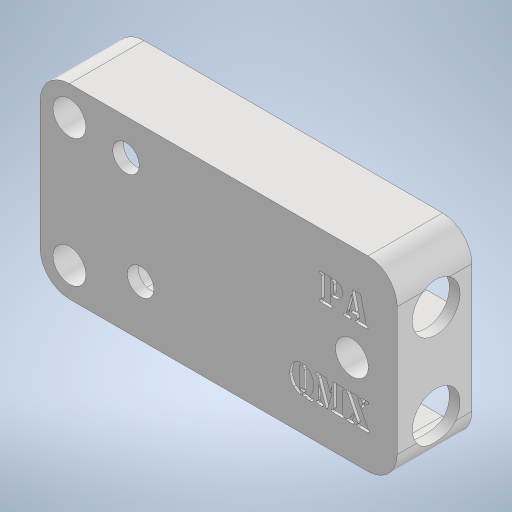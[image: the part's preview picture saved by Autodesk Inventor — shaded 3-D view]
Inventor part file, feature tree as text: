
AUTODESK INVENTOR PART (.ipt)
format: ipt  version: 2023 (Build 270158000, 158)  size: 636,416 bytes
history: native  units: in
note: dims shown in document units (in); Inventor stores cm internally (conversion verified against a paired STEP export)
features: sketch x9, reference x9, extrude x8, projected_geometry x5, other x4, plane x2, fillet x2
ambient origin geometry x8: Origin, YZ Plane, XZ Plane, XY Plane, X Axis, Y Axis, Z Axis, Center Point
bodies: Solid1 (feature_tree)
feature tree (39):
  extrude  "Extrusion1"  Depth=0.315in
  plane  "Work Plane1"
  sketch  "Sketch2"  dims[d3=0.4724in d4=0.0in d5=0.2441in]
  plane  "Work Plane2"
  extrude  "Extrusion2"  Depth=0.2441in
  extrude  "Extrusion3"  Depth=0.3937in
  fillet  "Fillet1"  Radius=0.3937in
  sketch  "Sketch4"  dims[d10=0.0787in d11=0.0787in d12=0.0in]
  sketch  "Sketch5"  dims[d13=0.3543in d14=0.3543in]
  extrude  "Extrusion4"  Depth=0.0787in TaperAngle=0.0deg
  extrude  "Extrusion5"  Depth=0.3543in
  extrude  "Extrusion6"  Depth=0.315in
  fillet  "Fillet2"  Radius=0.5906in
  extrude  "Extrusion7"  Depth=0.0787in
  extrude  "Extrusion8"  Depth=0.1969in
  sketch  "Sketch1"  dims[d0=0.4724in d1=0.0in d2=0.315in]
  reference  "Reference1"
  reference  "Reference2"
  reference  "Reference3"
  reference  "Reference4"
  projected_geometry  "Projected Loop1"
  sketch  "Sketch3"  dims[d6=0.2441in d7=0.2441in d8=0.3937in d9=0.0in]
  projected_geometry  "Projected Loop2"
  projected_geometry  "Projected Loop3"
  projected_geometry  "Projected Loop4"
  projected_geometry  "Projected Loop5"
  sketch  "Sketch6"  dims[d15=0.2338in d16=0.0in d17=0.315in d18=0.5906in]
  reference  "Reference5"
  reference  "Reference6"
  sketch  "Sketch7"  dims[d19=0.4537in d20=0.0in d21=0.0787in]
  reference  "Reference7"
  reference  "Reference8"
  reference  "Reference9"
  sketch  "Sketch8"  dims[d22=0.0197in d23=0.0in d24=0.1969in]
  sketch  "Sketch9"  dims[d25=0.1969in d26=0.3937in d27=0.0in]
  other  "<userpath>\Nextcloud2\private\HAMpower\Case\case_assambly.iam"
  other  "case_assambly.iam"
  other  "case_base:1"
  other  "powerplay:1"
